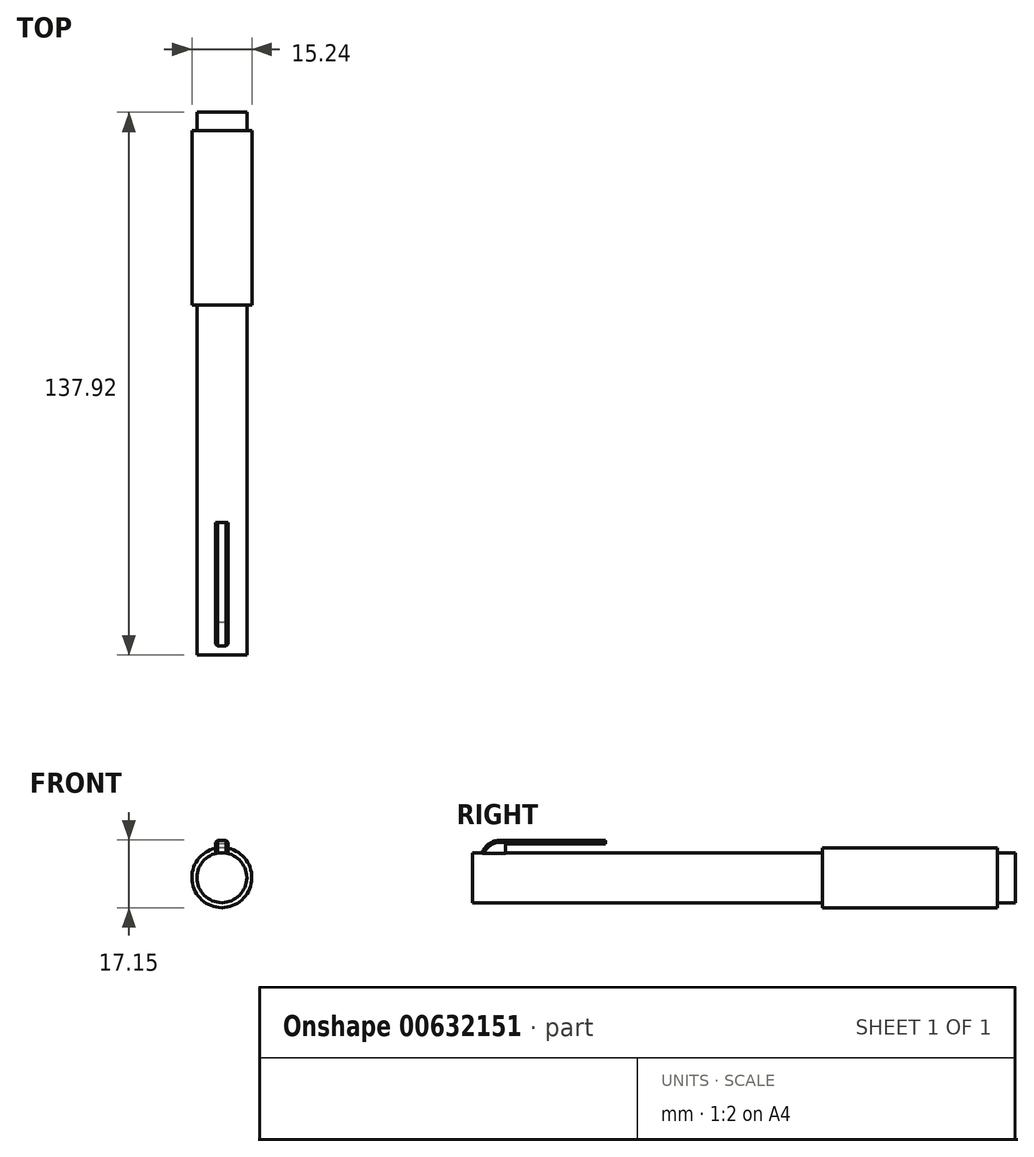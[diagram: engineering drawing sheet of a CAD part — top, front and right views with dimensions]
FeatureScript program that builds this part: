
annotation { "Feature Type Name" : "Feature", "Feature Type Description" : "" }
export const myFeature = defineFeature(function(context is Context, id is Id, definition is map)
    precondition{}
    {
        {
            var Q0;
            Q0=qCreatedBy(makeId("Right.planeOp"),FACE);
            var sketch = newSketch(context, id + "F0", { "sketchPlane" : qUnion([Q0])});
            skLineSegment(sketch, "E0", {"start": v(0, 6.35) * mm, "end": v(88.9, 6.35) * mm});
            skLineSegment(sketch, "E1", {"start": v(88.9, 6.35) * mm, "end": v(88.9, 7.62) * mm});
            skLineSegment(sketch, "E2", {"start": v(88.9, 7.62) * mm, "end": v(133.28, 7.62) * mm});
            skLineSegment(sketch, "E3", {"start": v(133.28, 7.62) * mm, "end": v(133.28, 6.35) * mm});
            skLineSegment(sketch, "E4", {"start": v(133.28, 6.35) * mm, "end": v(137.9, 6.35) * mm});
            skLineSegment(sketch, "E5", {"start": v(0, 6.35) * mm, "end": v(0, 0) * mm});
            skLineSegment(sketch, "E6", {"start": v(147.18, 6.35) * mm, "end": v(147.18, 0) * mm});
            skLineSegment(sketch, "E7", {"start": v(137.9, 6.35) * mm, "end": v(147.18, 3.46) * mm});
            skSolve(sketch);
        }
        {
            var Q0;
            Q0=qCreatedBy(makeId("Right.planeOp"),FACE);
            var sketch = newSketch(context, id + "F1", { "sketchPlane" : qUnion([Q0])});
            skLineSegment(sketch, "E8", {"start": v(158.3, 0) * mm, "end": v(0, 0) * mm});
            skSolve(sketch);
        }
        {
            var Q0;
            Q0=qCreatedBy(makeId("Top.planeOp"),FACE);
            var sketch = newSketch(context, id + "F2", { "sketchPlane" : qUnion([Q0])});
            skLineSegment(sketch, "E9.bottom", {"start": v(1.59, 2) * mm, "end": v(-1.59, 2) * mm});
            skLineSegment(sketch, "E9.top", {"start": v(1.59, 8.35) * mm, "end": v(-1.59, 8.35) * mm});
            skLineSegment(sketch, "E9.left", {"start": v(1.59, 2) * mm, "end": v(1.59, 8.35) * mm});
            skLineSegment(sketch, "E9.right", {"start": v(-1.59, 2) * mm, "end": v(-1.59, 8.35) * mm});
            skPoint(sketch, "E10", {"position": v(0, 2) * mm});
            skSolve(sketch);
        }
        {
            var Q0;
            Q0 = qSketchRegion(id + "F2", true);
            extrude(context, id + "F3", {"entities" : qUnion([Q0]), "depth" : 9.52 * mm, "offsetDistance" : 25.4 * mm});
        }
        {
            var Q0;
            Q0=makeQuery(id+"F3.opExtrude","SWEPT_FACE",FACE,{"disambiguationData":[OSD([sQuery(id+"F2.wireOp",EDGE,"E9.top")])]});
            var sketch = newSketch(context, id + "F4", { "sketchPlane" : qUnion([Q0])});
            skLineSegment(sketch, "E11.bottom", {"start": v(-1.59, 9.53) * mm, "end": v(1.59, 9.53) * mm});
            skLineSegment(sketch, "E11.top", {"start": v(-1.59, 8.6) * mm, "end": v(1.59, 8.6) * mm});
            skLineSegment(sketch, "E11.left", {"start": v(-1.59, 9.53) * mm, "end": v(-1.59, 8.6) * mm});
            skLineSegment(sketch, "E11.right", {"start": v(1.59, 9.53) * mm, "end": v(1.59, 8.6) * mm});
            skSolve(sketch);
        }
        {
            var Q0;
            Q0 = qSketchRegion(id + "F4", true);
            extrude(context, id + "F5", {"entities" : qUnion([Q0]), "operationType" : NewBodyOperationType.ADD, "depth" : 25.4 * mm, "offsetDistance" : 25.4 * mm});
        }
        {
            var Q0;
            Q0=makeQuery(id+"F5.opExtrude","CAP_EDGE",EDGE,{"disambiguationData":[OSD([sQuery(id+"F4.wireOp",EDGE,"E11.top")])],"isStart":true});
            var Q1;
            Q1=makeQuery(id+"F3.opExtrude","CAP_EDGE",EDGE,{"disambiguationData":[OSD([sQuery(id+"F2.wireOp",EDGE,"E9.bottom")])],"isStart":false});
            fillet(context, id + "F6", {"entities" : qUnion([Q0, Q1]), "radius" : 5.08 * mm, "tangentPropagation" : true, "allowEdgeOverflow" : false});
        }
        {
            var Q0;
            Q0=makeQuery(id+"F5.boolean.opBoolean","MERGE",EDGE,{"derivedFrom":[makeQuery(id+"F3.opExtrude","CAP_EDGE",EDGE,{"disambiguationData":[OSD([sQuery(id+"F2.wireOp",EDGE,"E9.left")])],"isStart":false}),makeQuery(id+"F5.opExtrude","SWEPT_EDGE",EDGE,{"disambiguationData":[OSD([sQuery(id+"F4.wireOp",EDGE,"E11.bottom"),sQuery(id+"F4.wireOp",EDGE,"E11.left")])]})]});
            var Q1;
            Q1=makeQuery(id+"F5.boolean.opBoolean","MERGE",EDGE,{"derivedFrom":[makeQuery(id+"F3.opExtrude","CAP_EDGE",EDGE,{"disambiguationData":[OSD([sQuery(id+"F2.wireOp",EDGE,"E9.right")])],"isStart":false}),makeQuery(id+"F5.opExtrude","SWEPT_EDGE",EDGE,{"disambiguationData":[OSD([sQuery(id+"F4.wireOp",EDGE,"E11.bottom"),sQuery(id+"F4.wireOp",EDGE,"E11.right")])]})]});
            chamfer(context, id + "F7", {"entities" : qUnion([Q0, Q1]), "width" : 0.5 * mm, "tangentPropagation" : true});
        }
        {
            var Q0;
            Q0=sQuery(id+"F0.wireOp",EDGE,"E7");
            var Q1;
            Q1=sQuery(id+"F0.wireOp",EDGE,"E2");
            var Q2;
            Q2=sQuery(id+"F0.wireOp",EDGE,"E0");
            var Q3;
            Q3=sQuery(id+"F0.wireOp",EDGE,"E5");
            var Q4;
            Q4=sQuery(id+"F0.wireOp",EDGE,"E1");
            var Q5;
            Q5=sQuery(id+"F0.wireOp",EDGE,"E3");
            var Q6;
            Q6=sQuery(id+"F0.wireOp",EDGE,"E4");
            var Q7;
            Q7=sQuery(id+"F1.wireOp",EDGE,"E8");
            revolve(context, id + "F8", {"bodyType" : ToolBodyType.SURFACE, "surfaceEntities" : qUnion([Q0, Q1, Q2, Q3, Q4, Q5, Q6]), "axis" : qUnion([Q7]), "revolveType" : RevolveType.FULL});
        }
        {
            var Q0;
            Q0=qCreatedBy(makeId("Front.planeOp"),FACE);
            var sketch = newSketch(context, id + "F9", { "sketchPlane" : qUnion([Q0])});
            skCircle(sketch, "E12", {"center": v(0, 0) * mm, "radius": 6.35 * mm});
            skSolve(sketch);
        }
        {
            var Q0;
            Q0 = qSketchRegion(id + "F9", true);
            extrude(context, id + "F10", {"entities" : qUnion([Q0]), "operationType" : NewBodyOperationType.ADD, "oppositeDirection" : true, "depth" : 137.92 * mm, "offsetDistance" : 25.4 * mm});
        }
        {
            var Q0;
            Q0=makeQuery(id+"F8.opRevolve","SWEPT_FACE",FACE,{"disambiguationData":[OSD([sQuery(id+"F0.wireOp",EDGE,"E1")])]});
            var sketch = newSketch(context, id + "F11", { "sketchPlane" : qUnion([Q0])});
            skCircle(sketch, "E13", {"center": v(0, 0) * mm, "radius": 7.62 * mm});
            skSolve(sketch);
        }
        {
            var Q0;
            Q0 = qSketchRegion(id + "F11", true);
            extrude(context, id + "F12", {"entities" : qUnion([Q0]), "operationType" : NewBodyOperationType.ADD, "oppositeDirection" : true, "depth" : 44.37 * mm, "offsetDistance" : 25.4 * mm});
        }
    });
